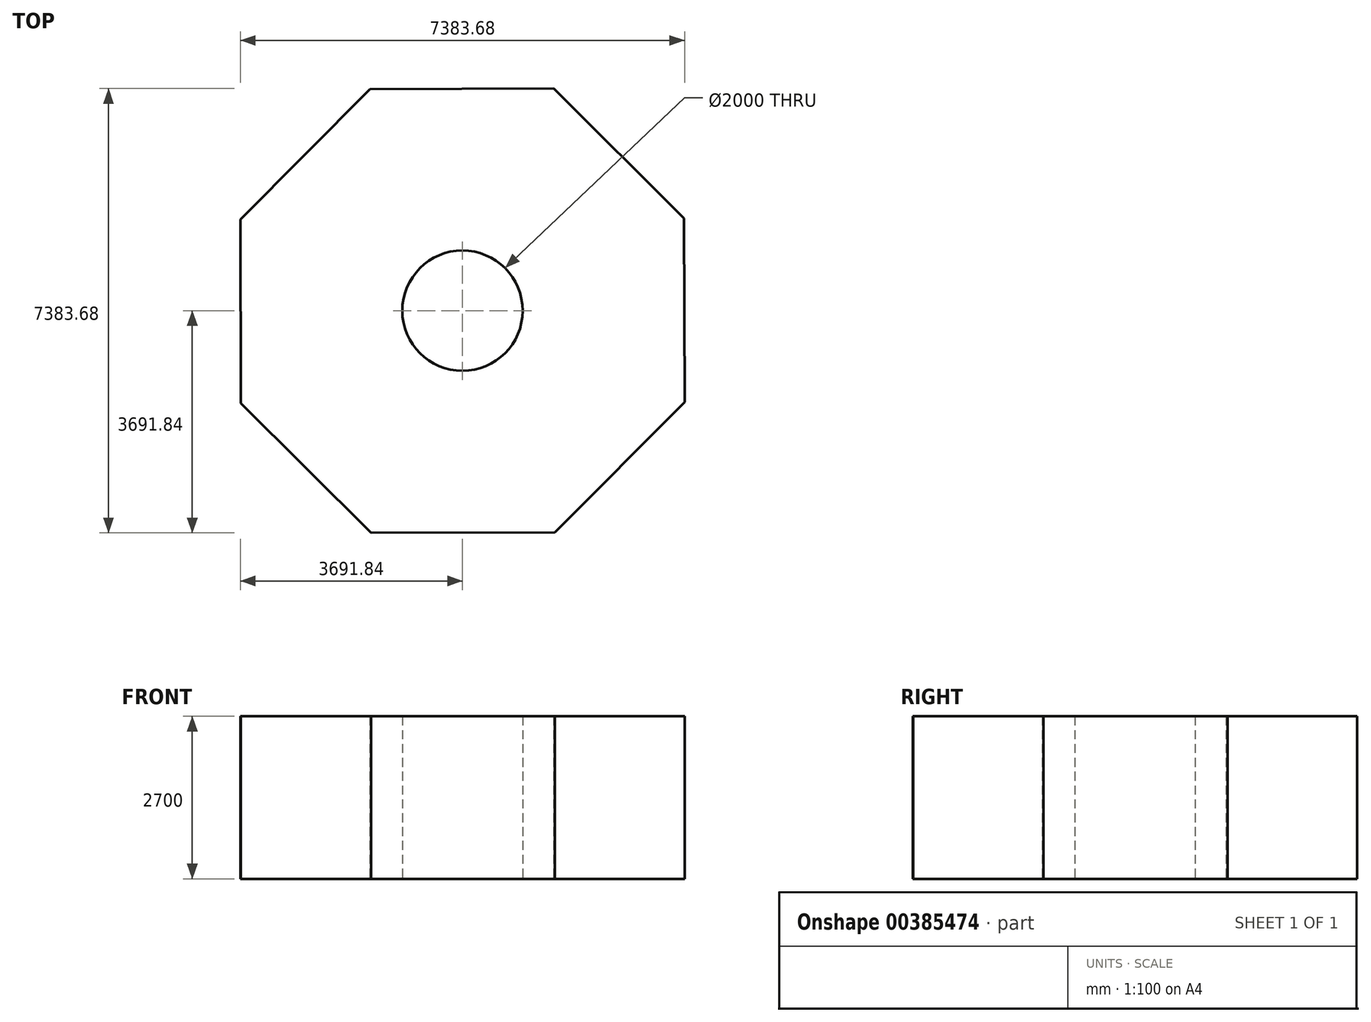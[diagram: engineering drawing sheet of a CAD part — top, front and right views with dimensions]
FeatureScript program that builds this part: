
annotation { "Feature Type Name" : "Feature", "Feature Type Description" : "" }
export const myFeature = defineFeature(function(context is Context, id is Id, definition is map)
    precondition{}
    {
        {
            var Q0;
            Q0=qCreatedBy(makeId("Top.planeOp"),FACE);
            var sketch = newSketch(context, id + "F0", { "sketchPlane" : qUnion([Q0])});
            skCircle(sketch, "E0.cCircle", {"center": v(0, 0) * mm, "radius": 3687.71 * mm, "construction": true});
            skLineSegment(sketch, "E0.0", {"start": v(-1517.5, -3691.84) * mm, "end": v(-3683.56, -1537.49) * mm});
            skLineSegment(sketch, "E0.1", {"start": v(-3683.56, -1537.49) * mm, "end": v(-3691.84, 1517.5) * mm});
            skLineSegment(sketch, "E0.2", {"start": v(-3691.84, 1517.5) * mm, "end": v(-1537.49, 3683.56) * mm});
            skLineSegment(sketch, "E0.3", {"start": v(-1537.49, 3683.56) * mm, "end": v(1517.5, 3691.84) * mm});
            skLineSegment(sketch, "E0.4", {"start": v(1517.5, 3691.84) * mm, "end": v(3683.56, 1537.49) * mm});
            skLineSegment(sketch, "E0.5", {"start": v(3683.56, 1537.49) * mm, "end": v(3691.84, -1517.5) * mm});
            skLineSegment(sketch, "E0.6", {"start": v(3691.84, -1517.5) * mm, "end": v(1537.49, -3683.56) * mm});
            skLineSegment(sketch, "E0.7", {"start": v(1537.49, -3683.56) * mm, "end": v(-1517.5, -3691.84) * mm});
            skPoint(sketch, "E0.0.midPoint", {"position": v(-2600.53, -2614.66) * mm});
            skCircle(sketch, "E1", {"center": v(0, 0) * mm, "radius": 1000 * mm});
            skSolve(sketch);
        }
        {
            var Q0;
            Q0=makeQuery(id+"F0.imprint","IMPRINT",FACE,{"disambiguationData":[TD([[makeQuery(id+"F0.imprint","IMPRINT",EDGE,{"derivedFrom":sQuery(id+"F0.wireOp",EDGE,"E0.0")}),-1.0]])]});
            extrude(context, id + "F1", {"entities" : qUnion([Q0]), "depth" : 2700 * mm});
        }
    });
